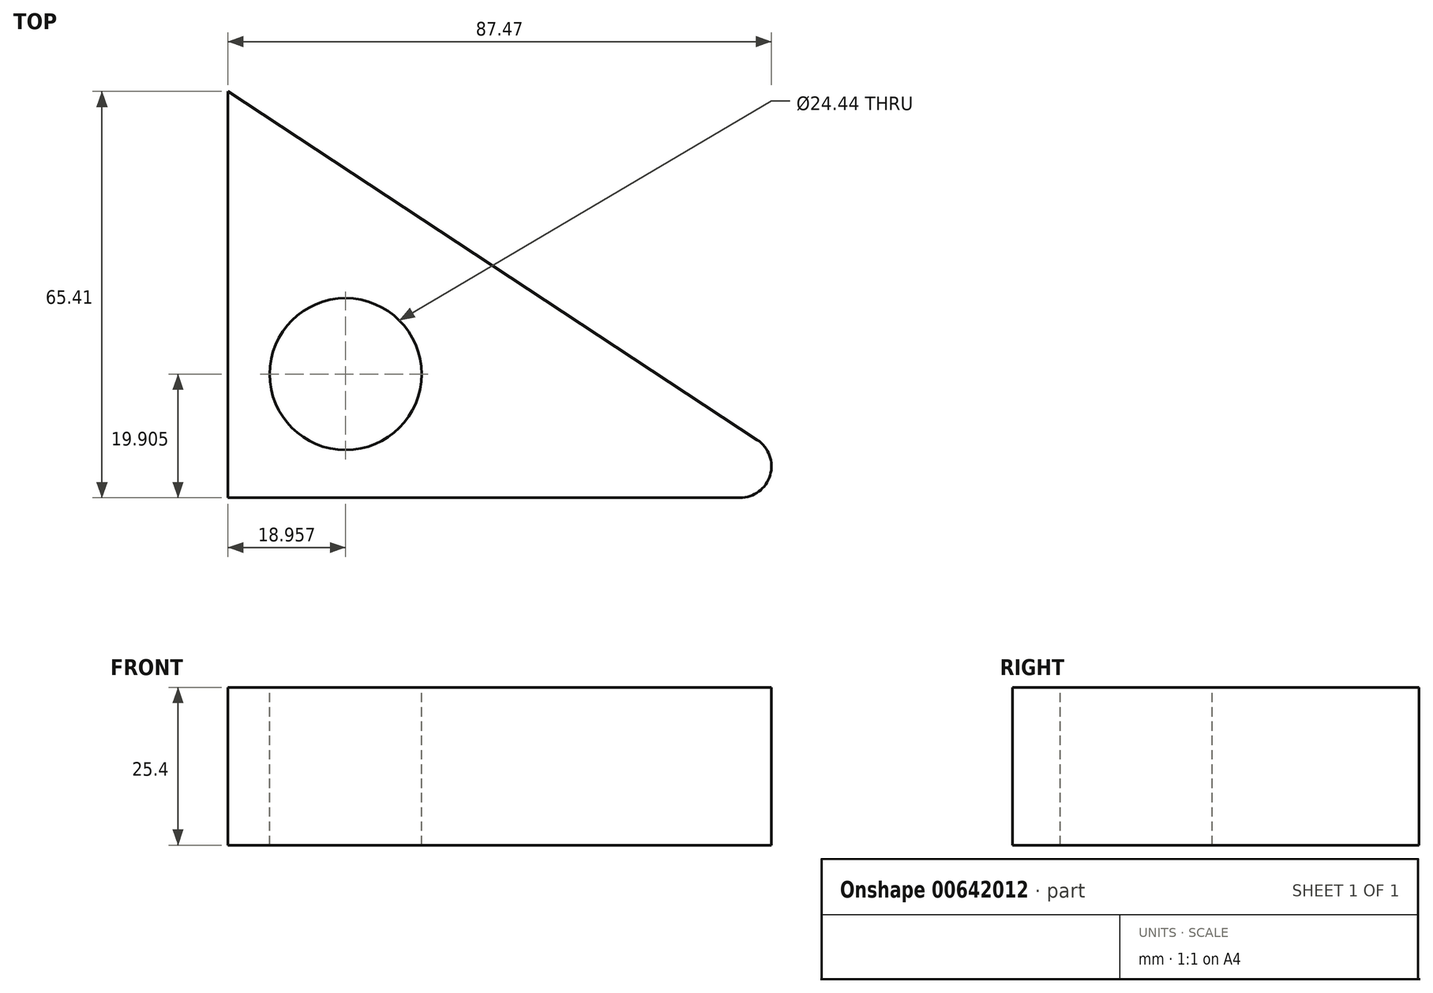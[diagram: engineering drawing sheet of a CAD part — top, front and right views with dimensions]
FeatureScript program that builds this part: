
annotation { "Feature Type Name" : "Feature", "Feature Type Description" : "" }
export const myFeature = defineFeature(function(context is Context, id is Id, definition is map)
    precondition{}
    {
        {
            var Q0;
            Q0=qCreatedBy(makeId("Top.planeOp"),FACE);
            var sketch = newSketch(context, id + "F0", { "sketchPlane" : qUnion([Q0])});
            skLineSegment(sketch, "E0", {"start": v(-48.25, 31.19) * mm, "end": v(-48.25, -34.22) * mm});
            skLineSegment(sketch, "E1", {"start": v(-48.25, -34.22) * mm, "end": v(51.1, -34.22) * mm});
            skLineSegment(sketch, "E2", {"start": v(51.1, -34.22) * mm, "end": v(-48.25, 31.19) * mm});
            skSolve(sketch);
        }
        {
            var Q0;
            Q0=makeQuery(id+"F0.imprint","IMPRINT",FACE,{"disambiguationData":[TD([[makeQuery(id+"F0.imprint","IMPRINT",EDGE,{"derivedFrom":sQuery(id+"F0.wireOp",EDGE,"E0")}),1.0]])]});
            extrude(context, id + "F1", {"entities" : qUnion([Q0]), "depth" : 25.4 * mm, "offsetDistance" : 25.4 * mm});
        }
        {
            var Q0;
            Q0=makeQuery(id+"F1.opExtrude","SWEPT_EDGE",EDGE,{"disambiguationData":[OSD([sQuery(id+"F0.wireOp",EDGE,"E1"),sQuery(id+"F0.wireOp",EDGE,"E2")])]});
            fillet(context, id + "F2", {"entities" : qUnion([Q0]), "radius" : 5.08 * mm, "tangentPropagation" : true, "allowEdgeOverflow" : false});
        }
        {
            var Q0;
            Q0=makeQuery(id+"F1.opExtrude","CAP_FACE",FACE,{"disambiguationData":[OSD([sQuery(id+"F0.wireOp",EDGE,"E0"),sQuery(id+"F0.wireOp",EDGE,"E1"),sQuery(id+"F0.wireOp",EDGE,"E2")])],"isStart":false});
            var sketch = newSketch(context, id + "F3", { "sketchPlane" : qUnion([Q0])});
            skCircle(sketch, "E3", {"center": v(-29.3, -14.31) * mm, "radius": 12.22 * mm});
            skSolve(sketch);
        }
        {
            var Q0;
            Q0 = qSketchRegion(id + "F3", true);
            extrude(context, id + "F4", {"entities" : qUnion([Q0]), "operationType" : NewBodyOperationType.REMOVE, "oppositeDirection" : true, "depth" : 25.4 * mm, "offsetDistance" : 25.4 * mm});
        }
    });
